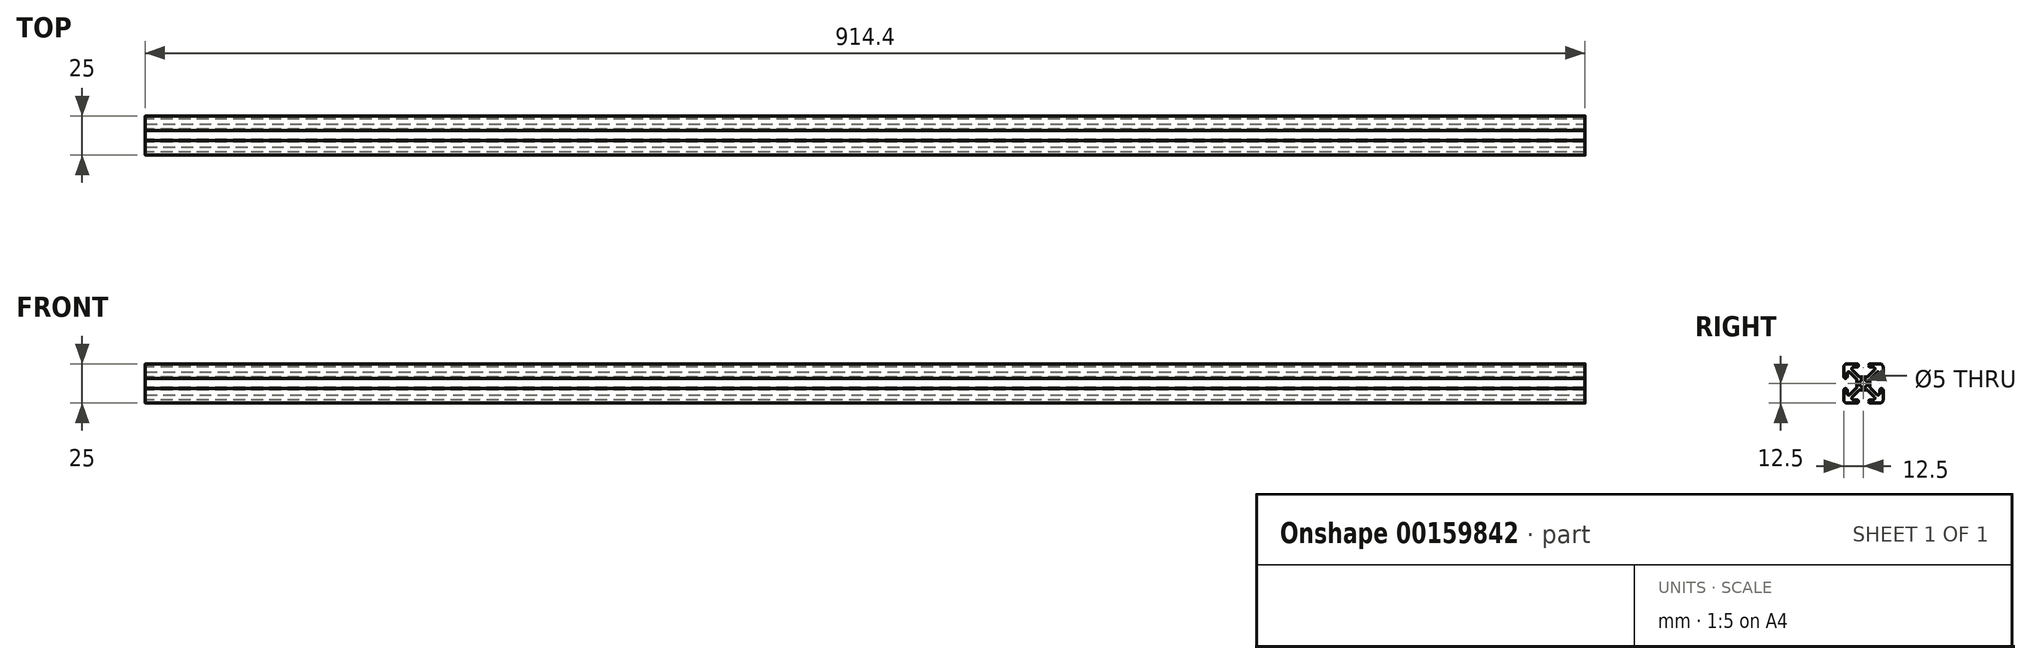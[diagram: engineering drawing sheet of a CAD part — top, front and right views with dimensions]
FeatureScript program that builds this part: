
annotation { "Feature Type Name" : "Feature", "Feature Type Description" : "" }
export const myFeature = defineFeature(function(context is Context, id is Id, definition is map)
    precondition{}
    {
        {
            var Q0;
            Q0=qCreatedBy(makeId("Right.planeOp"),FACE);
            var sketch = newSketch(context, id + "F0", { "sketchPlane" : qUnion([Q0])});
            skCircle(sketch, "E0", {"center": v(0, 0) * mm, "radius": 2.5 * mm});
            skLineSegment(sketch, "E1.bottom", {"start": v(4.05, -4.05) * mm, "end": v(-4.05, -4.05) * mm});
            skLineSegment(sketch, "E1.top", {"start": v(4.05, 4.05) * mm, "end": v(-4.05, 4.05) * mm});
            skLineSegment(sketch, "E1.left", {"start": v(4.05, -4.05) * mm, "end": v(4.05, 4.05) * mm});
            skLineSegment(sketch, "E1.right", {"start": v(-4.05, -4.05) * mm, "end": v(-4.05, 4.05) * mm});
            skLineSegment(sketch, "E2", {"start": v(0, 0) * mm, "end": v(4.05, 4.05) * mm, "construction": true});
            skLineSegment(sketch, "E3", {"start": v(2.54, 4.05) * mm, "end": v(8.85, 10.36) * mm});
            skLineSegment(sketch, "E4", {"start": v(8.85, 10.36) * mm, "end": v(3.25, 10.36) * mm});
            skLineSegment(sketch, "E5", {"start": v(3.25, 10.36) * mm, "end": v(3.25, 12.5) * mm});
            skLineSegment(sketch, "E6", {"start": v(3.25, 12.5) * mm, "end": v(12.5, 12.5) * mm});
            skLineSegment(sketch, "E7", {"start": v(12.5, 12.5) * mm, "end": v(12.5, 3.25) * mm});
            skLineSegment(sketch, "E8", {"start": v(12.5, 3.25) * mm, "end": v(10.36, 3.25) * mm});
            skLineSegment(sketch, "E9", {"start": v(10.36, 3.25) * mm, "end": v(10.36, 8.85) * mm});
            skLineSegment(sketch, "E10", {"start": v(10.36, 8.85) * mm, "end": v(4.05, 2.54) * mm});
            skLineSegment(sketch, "E11", {"start": v(3.36, 3.36) * mm, "end": v(14.33, 14.33) * mm, "construction": true});
            skLineSegment(sketch, "E12.MirrorCS", {"start": v(3.25, -10.36) * mm, "end": v(3.25, -12.5) * mm});
            skLineSegment(sketch, "E13.MirrorCS", {"start": v(12.5, -12.5) * mm, "end": v(12.5, -3.25) * mm});
            skLineSegment(sketch, "E14.MirrorCS", {"start": v(8.85, -10.36) * mm, "end": v(3.25, -10.36) * mm});
            skLineSegment(sketch, "E15.MirrorCS", {"start": v(12.5, -3.25) * mm, "end": v(10.36, -3.25) * mm});
            skLineSegment(sketch, "E16.MirrorCS", {"start": v(10.36, -3.25) * mm, "end": v(10.36, -8.85) * mm});
            skLineSegment(sketch, "E17.MirrorCS", {"start": v(3.25, -12.5) * mm, "end": v(12.5, -12.5) * mm});
            skLineSegment(sketch, "E18.MirrorCS", {"start": v(10.36, -8.85) * mm, "end": v(4.05, -2.54) * mm});
            skLineSegment(sketch, "E19.MirrorCS", {"start": v(3.36, -3.36) * mm, "end": v(14.33, -14.33) * mm, "construction": true});
            skLineSegment(sketch, "E20.MirrorCS", {"start": v(2.54, -4.05) * mm, "end": v(8.85, -10.36) * mm});
            skLineSegment(sketch, "E21.MirrorCS", {"start": v(-3.25, 10.36) * mm, "end": v(-3.25, 12.5) * mm});
            skLineSegment(sketch, "E22.MirrorCS", {"start": v(-8.85, 10.36) * mm, "end": v(-3.25, 10.36) * mm});
            skLineSegment(sketch, "E23.MirrorCS", {"start": v(-2.54, -4.05) * mm, "end": v(-8.85, -10.36) * mm});
            skLineSegment(sketch, "E24.MirrorCS", {"start": v(-10.36, -3.25) * mm, "end": v(-10.36, -8.85) * mm});
            skLineSegment(sketch, "E25.MirrorCS", {"start": v(-8.85, -10.36) * mm, "end": v(-3.25, -10.36) * mm});
            skLineSegment(sketch, "E26.MirrorCS", {"start": v(-10.36, 3.25) * mm, "end": v(-10.36, 8.85) * mm});
            skLineSegment(sketch, "E27.MirrorCS", {"start": v(-3.25, 12.5) * mm, "end": v(-12.5, 12.5) * mm});
            skLineSegment(sketch, "E28.MirrorCS", {"start": v(-10.36, 8.85) * mm, "end": v(-4.05, 2.54) * mm});
            skLineSegment(sketch, "E29.MirrorCS", {"start": v(-2.54, 4.05) * mm, "end": v(-8.85, 10.36) * mm});
            skLineSegment(sketch, "E30.MirrorCS", {"start": v(-10.36, -8.85) * mm, "end": v(-4.05, -2.54) * mm});
            skLineSegment(sketch, "E31.MirrorCS", {"start": v(-3.36, -3.36) * mm, "end": v(-14.33, -14.33) * mm, "construction": true});
            skLineSegment(sketch, "E32.MirrorCS", {"start": v(-12.5, -3.25) * mm, "end": v(-10.36, -3.25) * mm});
            skLineSegment(sketch, "E33.MirrorCS", {"start": v(-12.5, -12.5) * mm, "end": v(-12.5, -3.25) * mm});
            skLineSegment(sketch, "E34.MirrorCS", {"start": v(-3.25, -12.5) * mm, "end": v(-12.5, -12.5) * mm});
            skLineSegment(sketch, "E35.MirrorCS", {"start": v(-12.5, 3.25) * mm, "end": v(-10.36, 3.25) * mm});
            skLineSegment(sketch, "E36.MirrorCS", {"start": v(-3.36, 3.36) * mm, "end": v(-14.33, 14.33) * mm, "construction": true});
            skLineSegment(sketch, "E37.MirrorCS", {"start": v(-12.5, 12.5) * mm, "end": v(-12.5, 3.25) * mm});
            skLineSegment(sketch, "E38.MirrorCS", {"start": v(-3.25, -10.36) * mm, "end": v(-3.25, -12.5) * mm});
            skSolve(sketch);
        }
        {
            assignVariable(context, id + "F1", {"name" : "length", "anyValue" : 914.4 * mm});
        }
        {
            var Q0;
            Q0=makeQuery(id+"F0.imprint","IMPRINT",FACE,{"disambiguationData":[TD([[makeQuery(id+"F0.imprint","IMPRINT",EDGE,{"derivedFrom":sQuery(id+"F0.wireOp",EDGE,"E0")}),-1.0]])]});
            var Q1;
            Q1=makeQuery(id+"F0.imprint","IMPRINT",FACE,{"disambiguationData":[TD([[makeQuery(id+"F0.imprint","IMPRINT",EDGE,{"derivedFrom":sQuery(id+"F0.wireOp",EDGE,"E21.MirrorCS")}),1.0]])]});
            var Q2;
            {var subQ0=sQuery(id+"F0.wireOp",EDGE,"E3");Q2=makeQuery(id+"F0.imprint","IMPRINT",FACE,{"disambiguationData":[TD([[makeQuery(id+"F0.imprint","IMPRINT",EDGE,{"derivedFrom":subQ0}),-1.0]])]});}
            var Q3;
            {var subQ3=sQuery(id+"F0.wireOp",EDGE,"E23.MirrorCS");Q3=makeQuery(id+"F0.imprint","IMPRINT",FACE,{"disambiguationData":[TD([[makeQuery(id+"F0.imprint","IMPRINT",EDGE,{"derivedFrom":subQ3}),-1.0]])]});}
            var Q4;
            Q4=makeQuery(id+"F0.imprint","IMPRINT",FACE,{"disambiguationData":[TD([[makeQuery(id+"F0.imprint","IMPRINT",EDGE,{"derivedFrom":sQuery(id+"F0.wireOp",EDGE,"E12.MirrorCS")}),1.0]])]});
            extrude(context, id + "F2", {"entities" : qUnion([Q0, Q1, Q2, Q3, Q4]), "depth" : (getVariable(context, 'length'))});
        }
        {
            var Q0;
            Q0=makeQuery(id+"F2.opExtrude","SWEPT_EDGE",EDGE,{"disambiguationData":[OSD([sQuery(id+"F0.wireOp",EDGE,"E27.MirrorCS"),sQuery(id+"F0.wireOp",EDGE,"E37.MirrorCS")])]});
            var Q1;
            Q1=makeQuery(id+"F2.opExtrude","SWEPT_EDGE",EDGE,{"disambiguationData":[OSD([sQuery(id+"F0.wireOp",EDGE,"E6"),sQuery(id+"F0.wireOp",EDGE,"E7")])]});
            var Q2;
            Q2=makeQuery(id+"F2.opExtrude","SWEPT_EDGE",EDGE,{"disambiguationData":[OSD([sQuery(id+"F0.wireOp",EDGE,"E13.MirrorCS"),sQuery(id+"F0.wireOp",EDGE,"E17.MirrorCS")])]});
            var Q3;
            Q3=makeQuery(id+"F2.opExtrude","SWEPT_EDGE",EDGE,{"disambiguationData":[OSD([sQuery(id+"F0.wireOp",EDGE,"E33.MirrorCS"),sQuery(id+"F0.wireOp",EDGE,"E34.MirrorCS")])]});
            var Q4;
            Q4=makeQuery(id+"F2.opExtrude","SWEPT_EDGE",EDGE,{"disambiguationData":[OSD([sQuery(id+"F0.wireOp",EDGE,"E28.MirrorCS"),sQuery(id+"F0.wireOp",EDGE,"E1.right")])]});
            var Q5;
            Q5=makeQuery(id+"F2.opExtrude","SWEPT_EDGE",EDGE,{"disambiguationData":[OSD([sQuery(id+"F0.wireOp",EDGE,"E30.MirrorCS"),sQuery(id+"F0.wireOp",EDGE,"E1.right")])]});
            var Q6;
            Q6=makeQuery(id+"F2.opExtrude","SWEPT_EDGE",EDGE,{"disambiguationData":[OSD([sQuery(id+"F0.wireOp",EDGE,"E1.top"),sQuery(id+"F0.wireOp",EDGE,"E29.MirrorCS")])]});
            var Q7;
            Q7=makeQuery(id+"F2.opExtrude","SWEPT_EDGE",EDGE,{"disambiguationData":[OSD([sQuery(id+"F0.wireOp",EDGE,"E1.top"),sQuery(id+"F0.wireOp",EDGE,"E3")])]});
            var Q8;
            Q8=makeQuery(id+"F2.opExtrude","SWEPT_EDGE",EDGE,{"disambiguationData":[OSD([sQuery(id+"F0.wireOp",EDGE,"E1.left"),sQuery(id+"F0.wireOp",EDGE,"E10")])]});
            var Q9;
            Q9=makeQuery(id+"F2.opExtrude","SWEPT_EDGE",EDGE,{"disambiguationData":[OSD([sQuery(id+"F0.wireOp",EDGE,"E1.left"),sQuery(id+"F0.wireOp",EDGE,"E18.MirrorCS")])]});
            var Q10;
            Q10=makeQuery(id+"F2.opExtrude","SWEPT_EDGE",EDGE,{"disambiguationData":[OSD([sQuery(id+"F0.wireOp",EDGE,"E1.bottom"),sQuery(id+"F0.wireOp",EDGE,"E23.MirrorCS")])]});
            var Q11;
            Q11=makeQuery(id+"F2.opExtrude","SWEPT_EDGE",EDGE,{"disambiguationData":[OSD([sQuery(id+"F0.wireOp",EDGE,"E1.bottom"),sQuery(id+"F0.wireOp",EDGE,"E20.MirrorCS")])]});
            fillet(context, id + "F3", {"entities" : qUnion([Q0, Q1, Q2, Q3, Q4, Q5, Q6, Q7, Q8, Q9, Q10, Q11]), "radius" : 2.14 * mm, "tangentPropagation" : true, "allowEdgeOverflow" : false});
        }
        {
            var Q0;
            Q0=makeQuery(id+"F2.opExtrude","SWEPT_EDGE",EDGE,{"disambiguationData":[OSD([sQuery(id+"F0.wireOp",EDGE,"E35.MirrorCS"),sQuery(id+"F0.wireOp",EDGE,"E37.MirrorCS")])]});
            var Q1;
            Q1=makeQuery(id+"F2.opExtrude","SWEPT_EDGE",EDGE,{"disambiguationData":[OSD([sQuery(id+"F0.wireOp",EDGE,"E26.MirrorCS"),sQuery(id+"F0.wireOp",EDGE,"E35.MirrorCS")])]});
            var Q2;
            Q2=makeQuery(id+"F2.opExtrude","SWEPT_EDGE",EDGE,{"disambiguationData":[OSD([sQuery(id+"F0.wireOp",EDGE,"E21.MirrorCS"),sQuery(id+"F0.wireOp",EDGE,"E27.MirrorCS")])]});
            var Q3;
            Q3=makeQuery(id+"F2.opExtrude","SWEPT_EDGE",EDGE,{"disambiguationData":[OSD([sQuery(id+"F0.wireOp",EDGE,"E21.MirrorCS"),sQuery(id+"F0.wireOp",EDGE,"E22.MirrorCS")])]});
            var Q4;
            Q4=makeQuery(id+"F2.opExtrude","SWEPT_EDGE",EDGE,{"disambiguationData":[OSD([sQuery(id+"F0.wireOp",EDGE,"E5"),sQuery(id+"F0.wireOp",EDGE,"E6")])]});
            var Q5;
            Q5=makeQuery(id+"F2.opExtrude","SWEPT_EDGE",EDGE,{"disambiguationData":[OSD([sQuery(id+"F0.wireOp",EDGE,"E4"),sQuery(id+"F0.wireOp",EDGE,"E5")])]});
            var Q6;
            Q6=makeQuery(id+"F2.opExtrude","SWEPT_EDGE",EDGE,{"disambiguationData":[OSD([sQuery(id+"F0.wireOp",EDGE,"E8"),sQuery(id+"F0.wireOp",EDGE,"E9")])]});
            var Q7;
            Q7=makeQuery(id+"F2.opExtrude","SWEPT_EDGE",EDGE,{"disambiguationData":[OSD([sQuery(id+"F0.wireOp",EDGE,"E7"),sQuery(id+"F0.wireOp",EDGE,"E8")])]});
            var Q8;
            Q8=makeQuery(id+"F2.opExtrude","SWEPT_EDGE",EDGE,{"disambiguationData":[OSD([sQuery(id+"F0.wireOp",EDGE,"E15.MirrorCS"),sQuery(id+"F0.wireOp",EDGE,"E16.MirrorCS")])]});
            var Q9;
            Q9=makeQuery(id+"F2.opExtrude","SWEPT_EDGE",EDGE,{"disambiguationData":[OSD([sQuery(id+"F0.wireOp",EDGE,"E13.MirrorCS"),sQuery(id+"F0.wireOp",EDGE,"E15.MirrorCS")])]});
            var Q10;
            Q10=makeQuery(id+"F2.opExtrude","SWEPT_EDGE",EDGE,{"disambiguationData":[OSD([sQuery(id+"F0.wireOp",EDGE,"E12.MirrorCS"),sQuery(id+"F0.wireOp",EDGE,"E14.MirrorCS")])]});
            var Q11;
            Q11=makeQuery(id+"F2.opExtrude","SWEPT_EDGE",EDGE,{"disambiguationData":[OSD([sQuery(id+"F0.wireOp",EDGE,"E12.MirrorCS"),sQuery(id+"F0.wireOp",EDGE,"E17.MirrorCS")])]});
            var Q12;
            Q12=makeQuery(id+"F2.opExtrude","SWEPT_EDGE",EDGE,{"disambiguationData":[OSD([sQuery(id+"F0.wireOp",EDGE,"E25.MirrorCS"),sQuery(id+"F0.wireOp",EDGE,"E38.MirrorCS")])]});
            var Q13;
            Q13=makeQuery(id+"F2.opExtrude","SWEPT_EDGE",EDGE,{"disambiguationData":[OSD([sQuery(id+"F0.wireOp",EDGE,"E34.MirrorCS"),sQuery(id+"F0.wireOp",EDGE,"E38.MirrorCS")])]});
            var Q14;
            Q14=makeQuery(id+"F2.opExtrude","SWEPT_EDGE",EDGE,{"disambiguationData":[OSD([sQuery(id+"F0.wireOp",EDGE,"E26.MirrorCS"),sQuery(id+"F0.wireOp",EDGE,"E28.MirrorCS")])]});
            var Q15;
            Q15=makeQuery(id+"F2.opExtrude","SWEPT_EDGE",EDGE,{"disambiguationData":[OSD([sQuery(id+"F0.wireOp",EDGE,"E22.MirrorCS"),sQuery(id+"F0.wireOp",EDGE,"E29.MirrorCS")])]});
            var Q16;
            Q16=makeQuery(id+"F2.opExtrude","SWEPT_EDGE",EDGE,{"disambiguationData":[OSD([sQuery(id+"F0.wireOp",EDGE,"E3"),sQuery(id+"F0.wireOp",EDGE,"E4")])]});
            var Q17;
            Q17=makeQuery(id+"F2.opExtrude","SWEPT_EDGE",EDGE,{"disambiguationData":[OSD([sQuery(id+"F0.wireOp",EDGE,"E9"),sQuery(id+"F0.wireOp",EDGE,"E10")])]});
            var Q18;
            Q18=makeQuery(id+"F2.opExtrude","SWEPT_EDGE",EDGE,{"disambiguationData":[OSD([sQuery(id+"F0.wireOp",EDGE,"E14.MirrorCS"),sQuery(id+"F0.wireOp",EDGE,"E20.MirrorCS")])]});
            var Q19;
            Q19=makeQuery(id+"F2.opExtrude","SWEPT_EDGE",EDGE,{"disambiguationData":[OSD([sQuery(id+"F0.wireOp",EDGE,"E16.MirrorCS"),sQuery(id+"F0.wireOp",EDGE,"E18.MirrorCS")])]});
            var Q20;
            Q20=makeQuery(id+"F2.opExtrude","SWEPT_EDGE",EDGE,{"disambiguationData":[OSD([sQuery(id+"F0.wireOp",EDGE,"E23.MirrorCS"),sQuery(id+"F0.wireOp",EDGE,"E25.MirrorCS")])]});
            var Q21;
            Q21=makeQuery(id+"F2.opExtrude","SWEPT_EDGE",EDGE,{"disambiguationData":[OSD([sQuery(id+"F0.wireOp",EDGE,"E24.MirrorCS"),sQuery(id+"F0.wireOp",EDGE,"E30.MirrorCS")])]});
            var Q22;
            Q22=makeQuery(id+"F2.opExtrude","SWEPT_EDGE",EDGE,{"disambiguationData":[OSD([sQuery(id+"F0.wireOp",EDGE,"E24.MirrorCS"),sQuery(id+"F0.wireOp",EDGE,"E32.MirrorCS")])]});
            var Q23;
            Q23=makeQuery(id+"F2.opExtrude","SWEPT_EDGE",EDGE,{"disambiguationData":[OSD([sQuery(id+"F0.wireOp",EDGE,"E32.MirrorCS"),sQuery(id+"F0.wireOp",EDGE,"E33.MirrorCS")])]});
            fillet(context, id + "F4", {"entities" : qUnion([Q0, Q1, Q2, Q3, Q4, Q5, Q6, Q7, Q8, Q9, Q10, Q11, Q12, Q13, Q14, Q15, Q16, Q17, Q18, Q19, Q20, Q21, Q22, Q23]), "radius" : 1.07 * mm, "tangentPropagation" : true, "allowEdgeOverflow" : false});
        }
    });
